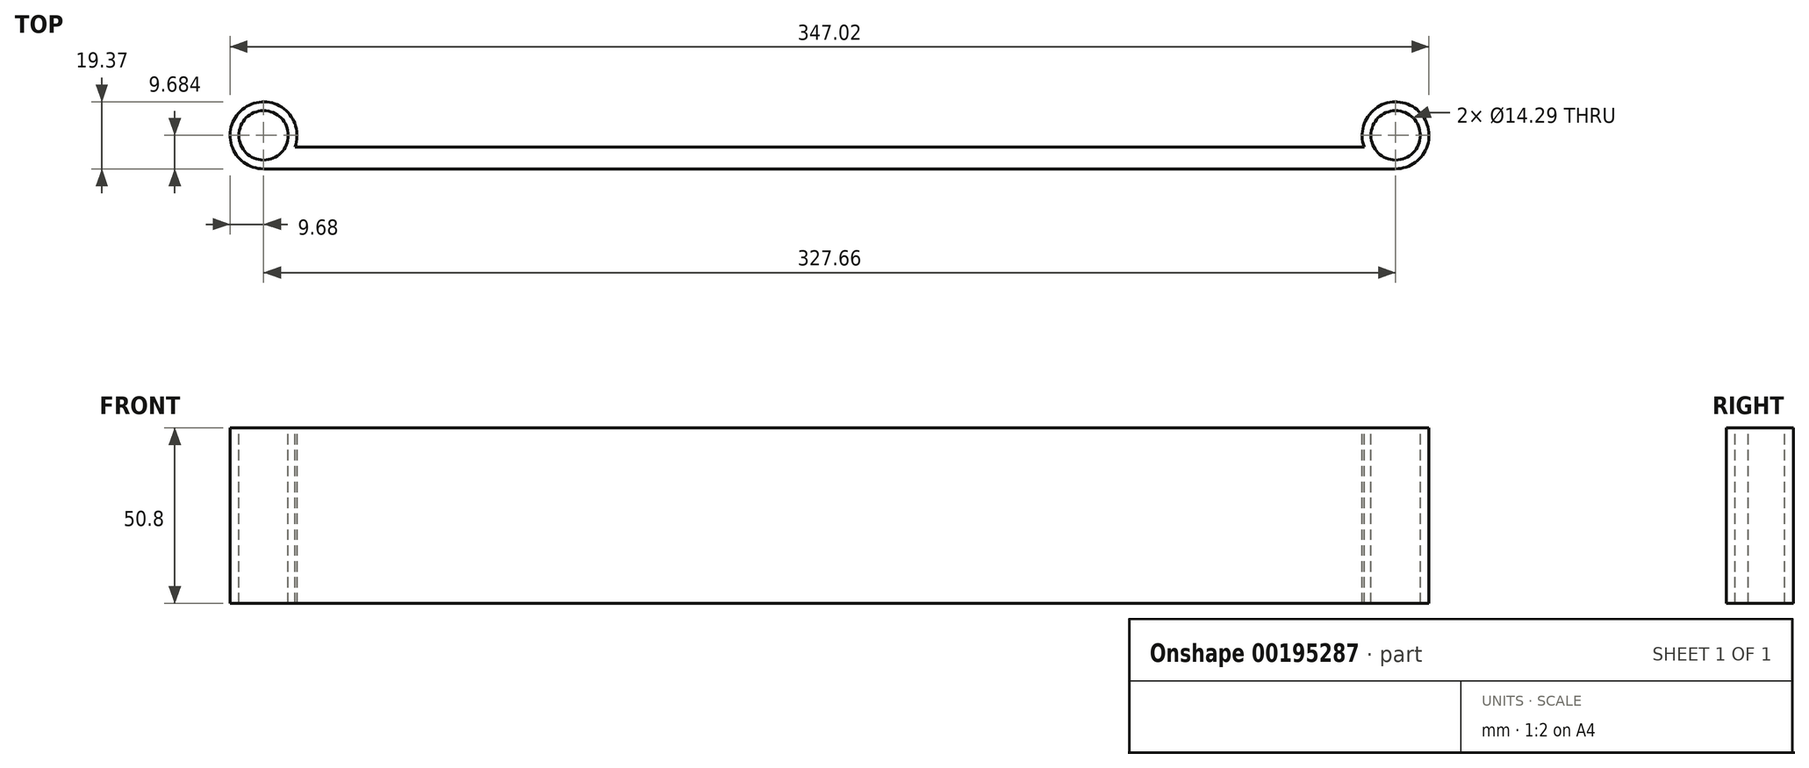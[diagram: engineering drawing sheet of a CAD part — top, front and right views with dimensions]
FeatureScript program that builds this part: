
annotation { "Feature Type Name" : "Feature", "Feature Type Description" : "" }
export const myFeature = defineFeature(function(context is Context, id is Id, definition is map)
    precondition{}
    {
        {
            var Q0;
            Q0=qCreatedBy(makeId("Top.planeOp"),FACE);
            var sketch = newSketch(context, id + "F0", { "sketchPlane" : qUnion([Q0])});
            skLineSegment(sketch, "E0.bottom", {"start": v(0, 0) * mm, "end": v(-156.11, 0) * mm});
            skLineSegment(sketch, "E0.top", {"start": v(0, 6.35) * mm, "end": v(-154.74, 6.35) * mm});
            skLineSegment(sketch, "E0.left", {"start": v(0, 0) * mm, "end": v(0, 6.35) * mm});
            skCircle(sketch, "E1", {"center": v(-163.83, 9.68) * mm, "radius": 7.14 * mm});
            skArc(sketch, "E2", {"start": v(-154.74, 6.35) * mm, "mid": v(-169.37, 17.62) * mm, "end": v(-163.83, 0) * mm});
            skLineSegment(sketch, "E3", {"start": v(-156.11, 0) * mm, "end": v(-205.07, 0) * mm, "construction": true});
            skLineSegment(sketch, "E4.trimOffspring", {"start": v(-157.9, 5.7) * mm, "end": v(-157.9, 6.35) * mm});
            skLineSegment(sketch, "E5.trimOffspring", {"start": v(-157.51, 6.35) * mm, "end": v(-157.9, 6.35) * mm});
            skLineSegment(sketch, "E6", {"start": v(-163.83, 0) * mm, "end": v(-156.11, 0) * mm});
            skLineSegment(sketch, "E7.MirrorCS", {"start": v(157.9, 5.7) * mm, "end": v(157.9, 6.35) * mm});
            skLineSegment(sketch, "E8.MirrorCS", {"start": v(157.51, 6.35) * mm, "end": v(157.9, 6.35) * mm});
            skLineSegment(sketch, "E9.MirrorCS", {"start": v(163.83, 0) * mm, "end": v(156.11, 0) * mm});
            skCircle(sketch, "E10.MirrorC", {"center": v(163.83, 9.68) * mm, "radius": 7.14 * mm});
            skArc(sketch, "E11.MirrorCS", {"start": v(154.74, 6.35) * mm, "mid": v(169.37, 17.62) * mm, "end": v(163.83, 0) * mm});
            skLineSegment(sketch, "E12.MirrorCS", {"start": v(0, 6.35) * mm, "end": v(154.74, 6.35) * mm});
            skLineSegment(sketch, "E13.MirrorCS", {"start": v(0, 0) * mm, "end": v(156.11, 0) * mm});
            skSolve(sketch);
        }
        {
            var Q0;
            Q0=makeQuery(id+"F0.imprint","IMPRINT",FACE,{"disambiguationData":[TD([[makeQuery(id+"F0.imprint","IMPRINT",EDGE,{"derivedFrom":sQuery(id+"F0.wireOp",EDGE,"E0.bottom")}),-1.0]])]});
            var Q1;
            Q1=makeQuery(id+"F0.imprint","IMPRINT",FACE,{"disambiguationData":[TD([[makeQuery(id+"F0.imprint","IMPRINT",EDGE,{"derivedFrom":sQuery(id+"F0.wireOp",EDGE,"E0.left")}),-1.0]])]});
            extrude(context, id + "F1", {"entities" : qUnion([Q0, Q1]), "oppositeDirection" : true, "depth" : 50.8 * mm});
        }
    });
